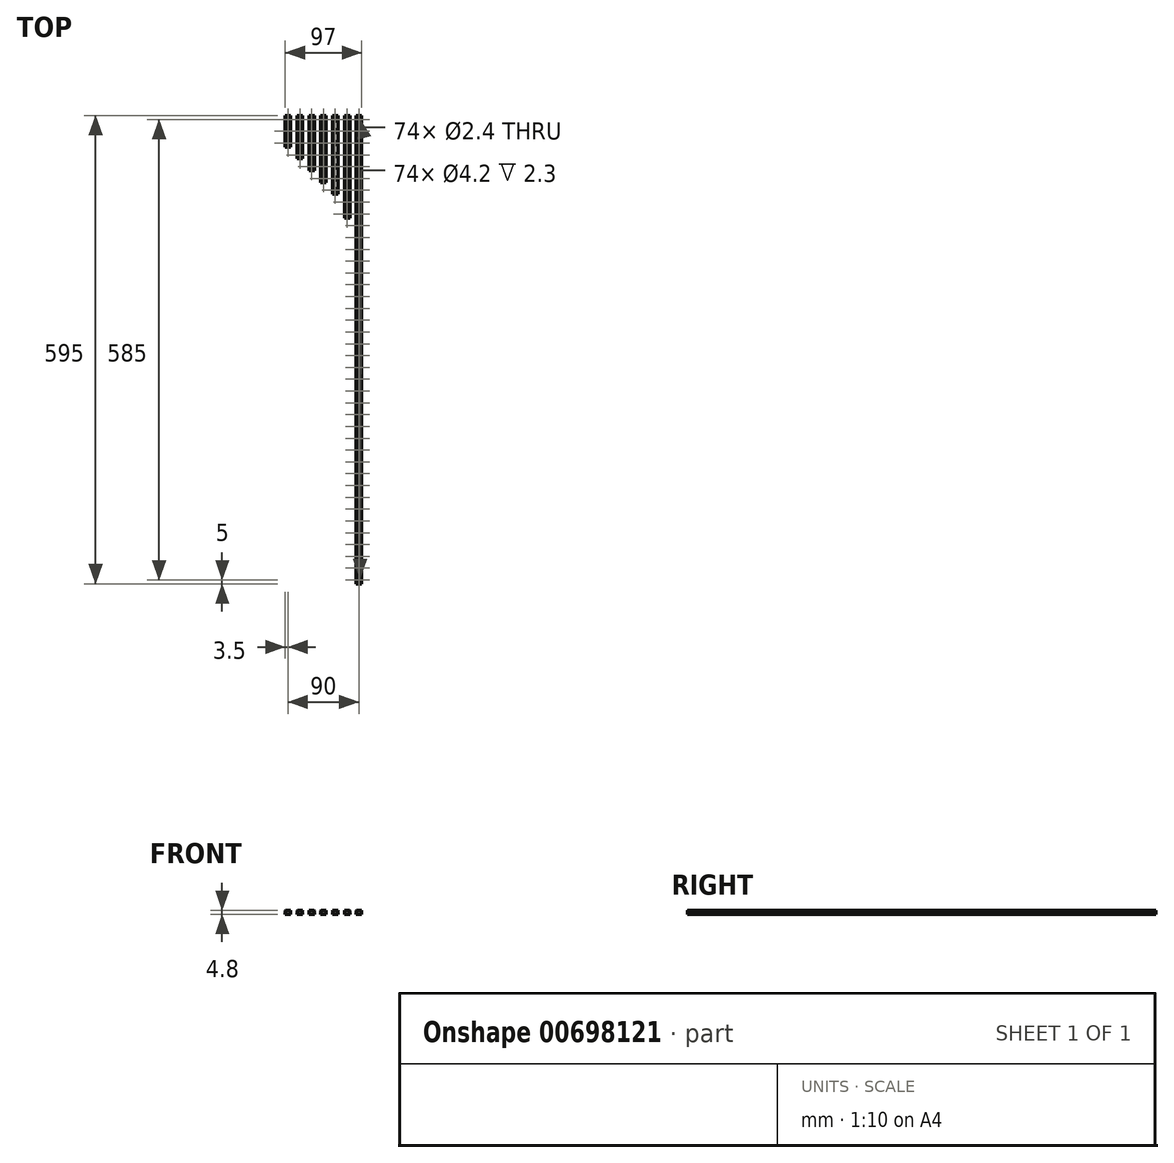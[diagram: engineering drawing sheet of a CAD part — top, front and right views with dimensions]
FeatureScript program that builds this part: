
annotation { "Feature Type Name" : "Feature", "Feature Type Description" : "" }
export const myFeature = defineFeature(function(context is Context, id is Id, definition is map)
    precondition{}
    {
        {
            var Q0;
            Q0=qCreatedBy(makeId("Front.planeOp"),FACE);
            var sketch = newSketch(context, id + "F0", { "sketchPlane" : qUnion([Q0])});
            skPoint(sketch, "E0.middle", {"position": v(0, 0) * mm});
            skLineSegment(sketch, "E1.bottom", {"start": v(3.22, -2.4) * mm, "end": v(-3.22, -2.4) * mm});
            skLineSegment(sketch, "E1.top", {"start": v(3.22, 2.4) * mm, "end": v(-3.22, 2.4) * mm});
            skLineSegment(sketch, "E1.left", {"start": v(3.5, -2.12) * mm, "end": v(3.5, 0.1) * mm});
            skLineSegment(sketch, "E1.right", {"start": v(-3.5, -2.12) * mm, "end": v(-3.5, 0.1) * mm});
            skArc(sketch, "E2", {"start": v(-3.5, 0.1) * mm, "mid": v(-3.23, 0.26) * mm, "end": v(-3.04, 0.51) * mm});
            skArc(sketch, "E3", {"start": v(3.5, 1.58) * mm, "mid": v(3.23, 1.42) * mm, "end": v(3.04, 1.17) * mm});
            skLineSegment(sketch, "E4", {"start": v(2.6, 1.16) * mm, "end": v(3.04, 1.16) * mm});
            skLineSegment(sketch, "E5", {"start": v(2.6, 0.51) * mm, "end": v(3.04, 0.51) * mm});
            skLineSegment(sketch, "E6", {"start": v(-2.6, 0.51) * mm, "end": v(-3.04, 0.51) * mm});
            skLineSegment(sketch, "E7", {"start": v(-2.6, 1.16) * mm, "end": v(-3.04, 1.16) * mm});
            skLineSegment(sketch, "E8", {"start": v(-3.5, 2.12) * mm, "end": v(-3.22, 2.4) * mm});
            skLineSegment(sketch, "E9.MirrorCS", {"start": v(3.5, 2.12) * mm, "end": v(3.22, 2.4) * mm});
            skLineSegment(sketch, "E10.MirrorCS", {"start": v(3.5, -2.12) * mm, "end": v(3.22, -2.4) * mm});
            skLineSegment(sketch, "E11.MirrorCS", {"start": v(-3.5, -2.12) * mm, "end": v(-3.22, -2.4) * mm});
            skPoint(sketch, "E12.orphan", {"position": v(-3.5, 2.4) * mm});
            skLineSegment(sketch, "E13.trimOffspring", {"start": v(-3.5, 1.58) * mm, "end": v(-3.5, 2.12) * mm});
            skArc(sketch, "E14.trimOffspring", {"start": v(-3.04, 1.17) * mm, "mid": v(-3.23, 1.42) * mm, "end": v(-3.5, 1.58) * mm});
            skPoint(sketch, "E15.orphan", {"position": v(3.5, 2.4) * mm});
            skLineSegment(sketch, "E16.trimOffspring", {"start": v(3.5, 1.58) * mm, "end": v(3.5, 2.12) * mm});
            skArc(sketch, "E17.trimOffspring", {"start": v(3.04, 0.51) * mm, "mid": v(3.23, 0.26) * mm, "end": v(3.5, 0.1) * mm});
            skPoint(sketch, "E18.orphan", {"position": v(3.5, -2.4) * mm});
            skPoint(sketch, "E19.orphan", {"position": v(-3.5, -2.4) * mm});
            skLineSegment(sketch, "E20", {"start": v(-2.6, 1.16) * mm, "end": v(-2.6, 0.51) * mm});
            skLineSegment(sketch, "E21", {"start": v(2.6, 1.16) * mm, "end": v(2.6, 0.51) * mm});
            skLineSegment(sketch, "E22", {"start": v(-3.74, 0.84) * mm, "end": v(3.74, 0.84) * mm, "construction": true});
            skLineSegment(sketch, "E23.1.0.0", {"start": v(11.26, 0.84) * mm, "end": v(18.74, 0.84) * mm, "construction": true});
            skLineSegment(sketch, "E23.1.0.1", {"start": v(11.5, -2.12) * mm, "end": v(11.5, 0.1) * mm});
            skLineSegment(sketch, "E23.1.0.2", {"start": v(18.5, -2.12) * mm, "end": v(18.5, 0.1) * mm});
            skLineSegment(sketch, "E23.1.0.3", {"start": v(18.22, -2.4) * mm, "end": v(11.78, -2.4) * mm});
            skLineSegment(sketch, "E23.1.0.4", {"start": v(18.22, 2.4) * mm, "end": v(11.78, 2.4) * mm});
            skPoint(sketch, "E23.1.0.5", {"position": v(15, 0) * mm});
            skPoint(sketch, "E23.1.0.6", {"position": v(11.5, -2.4) * mm});
            skPoint(sketch, "E23.1.0.7", {"position": v(11.5, 2.4) * mm});
            skPoint(sketch, "E23.1.0.8", {"position": v(18.5, 2.4) * mm});
            skPoint(sketch, "E23.1.0.9", {"position": v(18.5, -2.4) * mm});
            skPoint(sketch, "E23.1.0.10", {"position": v(15, 0) * mm});
            skLineSegment(sketch, "E23.1.0.11", {"start": v(18.5, -2.12) * mm, "end": v(18.22, -2.4) * mm});
            skLineSegment(sketch, "E23.1.0.12", {"start": v(18.5, 2.12) * mm, "end": v(18.22, 2.4) * mm});
            skLineSegment(sketch, "E23.1.0.13", {"start": v(11.5, -2.12) * mm, "end": v(11.78, -2.4) * mm});
            skLineSegment(sketch, "E23.1.0.14", {"start": v(12.4, 1.16) * mm, "end": v(11.96, 1.16) * mm});
            skLineSegment(sketch, "E23.1.0.15", {"start": v(11.5, 1.58) * mm, "end": v(11.5, 2.12) * mm});
            skLineSegment(sketch, "E23.1.0.16", {"start": v(18.5, 1.58) * mm, "end": v(18.5, 2.12) * mm});
            skArc(sketch, "E23.1.0.17", {"start": v(18.04, 0.51) * mm, "mid": v(18.23, 0.26) * mm, "end": v(18.5, 0.1) * mm});
            skLineSegment(sketch, "E23.1.0.18", {"start": v(12.4, 1.16) * mm, "end": v(12.4, 0.51) * mm});
            skLineSegment(sketch, "E23.1.0.19", {"start": v(17.6, 0.51) * mm, "end": v(18.04, 0.51) * mm});
            skLineSegment(sketch, "E23.1.0.20", {"start": v(12.4, 0.51) * mm, "end": v(11.96, 0.51) * mm});
            skArc(sketch, "E23.1.0.21", {"start": v(11.5, 0.1) * mm, "mid": v(11.77, 0.26) * mm, "end": v(11.96, 0.51) * mm});
            skLineSegment(sketch, "E23.1.0.22", {"start": v(11.5, 2.12) * mm, "end": v(11.78, 2.4) * mm});
            skArc(sketch, "E23.1.0.23", {"start": v(11.96, 1.17) * mm, "mid": v(11.77, 1.42) * mm, "end": v(11.5, 1.58) * mm});
            skLineSegment(sketch, "E23.1.0.24", {"start": v(17.6, 1.16) * mm, "end": v(18.04, 1.16) * mm});
            skArc(sketch, "E23.1.0.25", {"start": v(18.5, 1.58) * mm, "mid": v(18.23, 1.42) * mm, "end": v(18.04, 1.17) * mm});
            skArc(sketch, "E23.1.0.26", {"start": v(18.04, 0.51) * mm, "mid": v(18.23, 0.26) * mm, "end": v(18.5, 0.1) * mm});
            skLineSegment(sketch, "E23.1.0.27", {"start": v(17.6, 1.16) * mm, "end": v(17.6, 0.51) * mm});
            skLineSegment(sketch, "E23.2.0.0", {"start": v(26.26, 0.84) * mm, "end": v(33.74, 0.84) * mm, "construction": true});
            skLineSegment(sketch, "E23.2.0.1", {"start": v(26.5, -2.12) * mm, "end": v(26.5, 0.1) * mm});
            skLineSegment(sketch, "E23.2.0.2", {"start": v(33.5, -2.12) * mm, "end": v(33.5, 0.1) * mm});
            skLineSegment(sketch, "E23.2.0.3", {"start": v(33.22, -2.4) * mm, "end": v(26.78, -2.4) * mm});
            skLineSegment(sketch, "E23.2.0.4", {"start": v(33.22, 2.4) * mm, "end": v(26.78, 2.4) * mm});
            skPoint(sketch, "E23.2.0.5", {"position": v(30, 0) * mm});
            skPoint(sketch, "E23.2.0.6", {"position": v(26.5, -2.4) * mm});
            skPoint(sketch, "E23.2.0.7", {"position": v(26.5, 2.4) * mm});
            skPoint(sketch, "E23.2.0.8", {"position": v(33.5, 2.4) * mm});
            skPoint(sketch, "E23.2.0.9", {"position": v(33.5, -2.4) * mm});
            skPoint(sketch, "E23.2.0.10", {"position": v(30, 0) * mm});
            skLineSegment(sketch, "E23.2.0.11", {"start": v(33.5, -2.12) * mm, "end": v(33.22, -2.4) * mm});
            skLineSegment(sketch, "E23.2.0.12", {"start": v(33.5, 2.12) * mm, "end": v(33.22, 2.4) * mm});
            skLineSegment(sketch, "E23.2.0.13", {"start": v(26.5, -2.12) * mm, "end": v(26.78, -2.4) * mm});
            skLineSegment(sketch, "E23.2.0.14", {"start": v(27.4, 1.16) * mm, "end": v(26.96, 1.16) * mm});
            skLineSegment(sketch, "E23.2.0.15", {"start": v(26.5, 1.58) * mm, "end": v(26.5, 2.12) * mm});
            skLineSegment(sketch, "E23.2.0.16", {"start": v(33.5, 1.58) * mm, "end": v(33.5, 2.12) * mm});
            skArc(sketch, "E23.2.0.17", {"start": v(33.04, 0.51) * mm, "mid": v(33.23, 0.26) * mm, "end": v(33.5, 0.1) * mm});
            skLineSegment(sketch, "E23.2.0.18", {"start": v(27.4, 1.16) * mm, "end": v(27.4, 0.51) * mm});
            skLineSegment(sketch, "E23.2.0.19", {"start": v(32.6, 0.51) * mm, "end": v(33.04, 0.51) * mm});
            skLineSegment(sketch, "E23.2.0.20", {"start": v(27.4, 0.51) * mm, "end": v(26.96, 0.51) * mm});
            skArc(sketch, "E23.2.0.21", {"start": v(26.5, 0.1) * mm, "mid": v(26.77, 0.26) * mm, "end": v(26.96, 0.51) * mm});
            skLineSegment(sketch, "E23.2.0.22", {"start": v(26.5, 2.12) * mm, "end": v(26.78, 2.4) * mm});
            skArc(sketch, "E23.2.0.23", {"start": v(26.96, 1.17) * mm, "mid": v(26.77, 1.42) * mm, "end": v(26.5, 1.58) * mm});
            skLineSegment(sketch, "E23.2.0.24", {"start": v(32.6, 1.16) * mm, "end": v(33.04, 1.16) * mm});
            skArc(sketch, "E23.2.0.25", {"start": v(33.5, 1.58) * mm, "mid": v(33.23, 1.42) * mm, "end": v(33.04, 1.17) * mm});
            skArc(sketch, "E23.2.0.26", {"start": v(33.04, 0.51) * mm, "mid": v(33.23, 0.26) * mm, "end": v(33.5, 0.1) * mm});
            skLineSegment(sketch, "E23.2.0.27", {"start": v(32.6, 1.16) * mm, "end": v(32.6, 0.51) * mm});
            skLineSegment(sketch, "E23.3.0.0", {"start": v(41.26, 0.84) * mm, "end": v(48.74, 0.84) * mm, "construction": true});
            skLineSegment(sketch, "E23.3.0.1", {"start": v(41.5, -2.12) * mm, "end": v(41.5, 0.1) * mm});
            skLineSegment(sketch, "E23.3.0.2", {"start": v(48.5, -2.12) * mm, "end": v(48.5, 0.1) * mm});
            skLineSegment(sketch, "E23.3.0.3", {"start": v(48.22, -2.4) * mm, "end": v(41.78, -2.4) * mm});
            skLineSegment(sketch, "E23.3.0.4", {"start": v(48.22, 2.4) * mm, "end": v(41.78, 2.4) * mm});
            skPoint(sketch, "E23.3.0.5", {"position": v(45, 0) * mm});
            skPoint(sketch, "E23.3.0.6", {"position": v(41.5, -2.4) * mm});
            skPoint(sketch, "E23.3.0.7", {"position": v(41.5, 2.4) * mm});
            skPoint(sketch, "E23.3.0.8", {"position": v(48.5, 2.4) * mm});
            skPoint(sketch, "E23.3.0.9", {"position": v(48.5, -2.4) * mm});
            skPoint(sketch, "E23.3.0.10", {"position": v(45, 0) * mm});
            skLineSegment(sketch, "E23.3.0.11", {"start": v(48.5, -2.12) * mm, "end": v(48.22, -2.4) * mm});
            skLineSegment(sketch, "E23.3.0.12", {"start": v(48.5, 2.12) * mm, "end": v(48.22, 2.4) * mm});
            skLineSegment(sketch, "E23.3.0.13", {"start": v(41.5, -2.12) * mm, "end": v(41.78, -2.4) * mm});
            skLineSegment(sketch, "E23.3.0.14", {"start": v(42.4, 1.16) * mm, "end": v(41.96, 1.16) * mm});
            skLineSegment(sketch, "E23.3.0.15", {"start": v(41.5, 1.58) * mm, "end": v(41.5, 2.12) * mm});
            skLineSegment(sketch, "E23.3.0.16", {"start": v(48.5, 1.58) * mm, "end": v(48.5, 2.12) * mm});
            skArc(sketch, "E23.3.0.17", {"start": v(48.04, 0.51) * mm, "mid": v(48.23, 0.26) * mm, "end": v(48.5, 0.1) * mm});
            skLineSegment(sketch, "E23.3.0.18", {"start": v(42.4, 1.16) * mm, "end": v(42.4, 0.51) * mm});
            skLineSegment(sketch, "E23.3.0.19", {"start": v(47.6, 0.51) * mm, "end": v(48.04, 0.51) * mm});
            skLineSegment(sketch, "E23.3.0.20", {"start": v(42.4, 0.51) * mm, "end": v(41.96, 0.51) * mm});
            skArc(sketch, "E23.3.0.21", {"start": v(41.5, 0.1) * mm, "mid": v(41.77, 0.26) * mm, "end": v(41.96, 0.51) * mm});
            skLineSegment(sketch, "E23.3.0.22", {"start": v(41.5, 2.12) * mm, "end": v(41.78, 2.4) * mm});
            skArc(sketch, "E23.3.0.23", {"start": v(41.96, 1.17) * mm, "mid": v(41.77, 1.42) * mm, "end": v(41.5, 1.58) * mm});
            skLineSegment(sketch, "E23.3.0.24", {"start": v(47.6, 1.16) * mm, "end": v(48.04, 1.16) * mm});
            skArc(sketch, "E23.3.0.25", {"start": v(48.5, 1.58) * mm, "mid": v(48.23, 1.42) * mm, "end": v(48.04, 1.17) * mm});
            skArc(sketch, "E23.3.0.26", {"start": v(48.04, 0.51) * mm, "mid": v(48.23, 0.26) * mm, "end": v(48.5, 0.1) * mm});
            skLineSegment(sketch, "E23.3.0.27", {"start": v(47.6, 1.16) * mm, "end": v(47.6, 0.51) * mm});
            skLineSegment(sketch, "E23.4.0.0", {"start": v(56.26, 0.84) * mm, "end": v(63.74, 0.84) * mm, "construction": true});
            skLineSegment(sketch, "E23.4.0.1", {"start": v(56.5, -2.12) * mm, "end": v(56.5, 0.1) * mm});
            skLineSegment(sketch, "E23.4.0.2", {"start": v(63.5, -2.12) * mm, "end": v(63.5, 0.1) * mm});
            skLineSegment(sketch, "E23.4.0.3", {"start": v(63.22, -2.4) * mm, "end": v(56.78, -2.4) * mm});
            skLineSegment(sketch, "E23.4.0.4", {"start": v(63.22, 2.4) * mm, "end": v(56.78, 2.4) * mm});
            skPoint(sketch, "E23.4.0.5", {"position": v(60, 0) * mm});
            skPoint(sketch, "E23.4.0.6", {"position": v(56.5, -2.4) * mm});
            skPoint(sketch, "E23.4.0.7", {"position": v(56.5, 2.4) * mm});
            skPoint(sketch, "E23.4.0.8", {"position": v(63.5, 2.4) * mm});
            skPoint(sketch, "E23.4.0.9", {"position": v(63.5, -2.4) * mm});
            skPoint(sketch, "E23.4.0.10", {"position": v(60, 0) * mm});
            skLineSegment(sketch, "E23.4.0.11", {"start": v(63.5, -2.12) * mm, "end": v(63.22, -2.4) * mm});
            skLineSegment(sketch, "E23.4.0.12", {"start": v(63.5, 2.12) * mm, "end": v(63.22, 2.4) * mm});
            skLineSegment(sketch, "E23.4.0.13", {"start": v(56.5, -2.12) * mm, "end": v(56.78, -2.4) * mm});
            skLineSegment(sketch, "E23.4.0.14", {"start": v(57.4, 1.16) * mm, "end": v(56.96, 1.16) * mm});
            skLineSegment(sketch, "E23.4.0.15", {"start": v(56.5, 1.58) * mm, "end": v(56.5, 2.12) * mm});
            skLineSegment(sketch, "E23.4.0.16", {"start": v(63.5, 1.58) * mm, "end": v(63.5, 2.12) * mm});
            skArc(sketch, "E23.4.0.17", {"start": v(63.04, 0.51) * mm, "mid": v(63.23, 0.26) * mm, "end": v(63.5, 0.1) * mm});
            skLineSegment(sketch, "E23.4.0.18", {"start": v(57.4, 1.16) * mm, "end": v(57.4, 0.51) * mm});
            skLineSegment(sketch, "E23.4.0.19", {"start": v(62.6, 0.51) * mm, "end": v(63.04, 0.51) * mm});
            skLineSegment(sketch, "E23.4.0.20", {"start": v(57.4, 0.51) * mm, "end": v(56.96, 0.51) * mm});
            skArc(sketch, "E23.4.0.21", {"start": v(56.5, 0.1) * mm, "mid": v(56.77, 0.26) * mm, "end": v(56.96, 0.51) * mm});
            skLineSegment(sketch, "E23.4.0.22", {"start": v(56.5, 2.12) * mm, "end": v(56.78, 2.4) * mm});
            skArc(sketch, "E23.4.0.23", {"start": v(56.96, 1.17) * mm, "mid": v(56.77, 1.42) * mm, "end": v(56.5, 1.58) * mm});
            skLineSegment(sketch, "E23.4.0.24", {"start": v(62.6, 1.16) * mm, "end": v(63.04, 1.16) * mm});
            skArc(sketch, "E23.4.0.25", {"start": v(63.5, 1.58) * mm, "mid": v(63.23, 1.42) * mm, "end": v(63.04, 1.17) * mm});
            skArc(sketch, "E23.4.0.26", {"start": v(63.04, 0.51) * mm, "mid": v(63.23, 0.26) * mm, "end": v(63.5, 0.1) * mm});
            skLineSegment(sketch, "E23.4.0.27", {"start": v(62.6, 1.16) * mm, "end": v(62.6, 0.51) * mm});
            skLineSegment(sketch, "E23.5.0.0", {"start": v(71.26, 0.84) * mm, "end": v(78.74, 0.84) * mm, "construction": true});
            skLineSegment(sketch, "E23.5.0.1", {"start": v(71.5, -2.12) * mm, "end": v(71.5, 0.1) * mm});
            skLineSegment(sketch, "E23.5.0.2", {"start": v(78.5, -2.12) * mm, "end": v(78.5, 0.1) * mm});
            skLineSegment(sketch, "E23.5.0.3", {"start": v(78.22, -2.4) * mm, "end": v(71.78, -2.4) * mm});
            skLineSegment(sketch, "E23.5.0.4", {"start": v(78.22, 2.4) * mm, "end": v(71.78, 2.4) * mm});
            skPoint(sketch, "E23.5.0.5", {"position": v(75, 0) * mm});
            skPoint(sketch, "E23.5.0.6", {"position": v(71.5, -2.4) * mm});
            skPoint(sketch, "E23.5.0.7", {"position": v(71.5, 2.4) * mm});
            skPoint(sketch, "E23.5.0.8", {"position": v(78.5, 2.4) * mm});
            skPoint(sketch, "E23.5.0.9", {"position": v(78.5, -2.4) * mm});
            skPoint(sketch, "E23.5.0.10", {"position": v(75, 0) * mm});
            skLineSegment(sketch, "E23.5.0.11", {"start": v(78.5, -2.12) * mm, "end": v(78.22, -2.4) * mm});
            skLineSegment(sketch, "E23.5.0.12", {"start": v(78.5, 2.12) * mm, "end": v(78.22, 2.4) * mm});
            skLineSegment(sketch, "E23.5.0.13", {"start": v(71.5, -2.12) * mm, "end": v(71.78, -2.4) * mm});
            skLineSegment(sketch, "E23.5.0.14", {"start": v(72.4, 1.16) * mm, "end": v(71.96, 1.16) * mm});
            skLineSegment(sketch, "E23.5.0.15", {"start": v(71.5, 1.58) * mm, "end": v(71.5, 2.12) * mm});
            skLineSegment(sketch, "E23.5.0.16", {"start": v(78.5, 1.58) * mm, "end": v(78.5, 2.12) * mm});
            skArc(sketch, "E23.5.0.17", {"start": v(78.04, 0.51) * mm, "mid": v(78.23, 0.26) * mm, "end": v(78.5, 0.1) * mm});
            skLineSegment(sketch, "E23.5.0.18", {"start": v(72.4, 1.16) * mm, "end": v(72.4, 0.51) * mm});
            skLineSegment(sketch, "E23.5.0.19", {"start": v(77.6, 0.51) * mm, "end": v(78.04, 0.51) * mm});
            skLineSegment(sketch, "E23.5.0.20", {"start": v(72.4, 0.51) * mm, "end": v(71.96, 0.51) * mm});
            skArc(sketch, "E23.5.0.21", {"start": v(71.5, 0.1) * mm, "mid": v(71.77, 0.26) * mm, "end": v(71.96, 0.51) * mm});
            skLineSegment(sketch, "E23.5.0.22", {"start": v(71.5, 2.12) * mm, "end": v(71.78, 2.4) * mm});
            skArc(sketch, "E23.5.0.23", {"start": v(71.96, 1.17) * mm, "mid": v(71.77, 1.42) * mm, "end": v(71.5, 1.58) * mm});
            skLineSegment(sketch, "E23.5.0.24", {"start": v(77.6, 1.16) * mm, "end": v(78.04, 1.16) * mm});
            skArc(sketch, "E23.5.0.25", {"start": v(78.5, 1.58) * mm, "mid": v(78.23, 1.42) * mm, "end": v(78.04, 1.17) * mm});
            skArc(sketch, "E23.5.0.26", {"start": v(78.04, 0.51) * mm, "mid": v(78.23, 0.26) * mm, "end": v(78.5, 0.1) * mm});
            skLineSegment(sketch, "E23.5.0.27", {"start": v(77.6, 1.16) * mm, "end": v(77.6, 0.51) * mm});
            skLineSegment(sketch, "E23.6.0.0", {"start": v(86.26, 0.84) * mm, "end": v(93.74, 0.84) * mm, "construction": true});
            skLineSegment(sketch, "E23.6.0.1", {"start": v(86.5, -2.12) * mm, "end": v(86.5, 0.1) * mm});
            skLineSegment(sketch, "E23.6.0.2", {"start": v(93.5, -2.12) * mm, "end": v(93.5, 0.1) * mm});
            skLineSegment(sketch, "E23.6.0.3", {"start": v(93.22, -2.4) * mm, "end": v(86.78, -2.4) * mm});
            skLineSegment(sketch, "E23.6.0.4", {"start": v(93.22, 2.4) * mm, "end": v(86.78, 2.4) * mm});
            skPoint(sketch, "E23.6.0.5", {"position": v(90, 0) * mm});
            skPoint(sketch, "E23.6.0.6", {"position": v(86.5, -2.4) * mm});
            skPoint(sketch, "E23.6.0.7", {"position": v(86.5, 2.4) * mm});
            skPoint(sketch, "E23.6.0.8", {"position": v(93.5, 2.4) * mm});
            skPoint(sketch, "E23.6.0.9", {"position": v(93.5, -2.4) * mm});
            skPoint(sketch, "E23.6.0.10", {"position": v(90, 0) * mm});
            skLineSegment(sketch, "E23.6.0.11", {"start": v(93.5, -2.12) * mm, "end": v(93.22, -2.4) * mm});
            skLineSegment(sketch, "E23.6.0.12", {"start": v(93.5, 2.12) * mm, "end": v(93.22, 2.4) * mm});
            skLineSegment(sketch, "E23.6.0.13", {"start": v(86.5, -2.12) * mm, "end": v(86.78, -2.4) * mm});
            skLineSegment(sketch, "E23.6.0.14", {"start": v(87.4, 1.16) * mm, "end": v(86.96, 1.16) * mm});
            skLineSegment(sketch, "E23.6.0.15", {"start": v(86.5, 1.58) * mm, "end": v(86.5, 2.12) * mm});
            skLineSegment(sketch, "E23.6.0.16", {"start": v(93.5, 1.58) * mm, "end": v(93.5, 2.12) * mm});
            skArc(sketch, "E23.6.0.17", {"start": v(93.04, 0.51) * mm, "mid": v(93.23, 0.26) * mm, "end": v(93.5, 0.1) * mm});
            skLineSegment(sketch, "E23.6.0.18", {"start": v(87.4, 1.16) * mm, "end": v(87.4, 0.51) * mm});
            skLineSegment(sketch, "E23.6.0.19", {"start": v(92.6, 0.51) * mm, "end": v(93.04, 0.51) * mm});
            skLineSegment(sketch, "E23.6.0.20", {"start": v(87.4, 0.51) * mm, "end": v(86.96, 0.51) * mm});
            skArc(sketch, "E23.6.0.21", {"start": v(86.5, 0.1) * mm, "mid": v(86.77, 0.26) * mm, "end": v(86.96, 0.51) * mm});
            skLineSegment(sketch, "E23.6.0.22", {"start": v(86.5, 2.12) * mm, "end": v(86.78, 2.4) * mm});
            skArc(sketch, "E23.6.0.23", {"start": v(86.96, 1.17) * mm, "mid": v(86.77, 1.42) * mm, "end": v(86.5, 1.58) * mm});
            skLineSegment(sketch, "E23.6.0.24", {"start": v(92.6, 1.16) * mm, "end": v(93.04, 1.16) * mm});
            skArc(sketch, "E23.6.0.25", {"start": v(93.5, 1.58) * mm, "mid": v(93.23, 1.42) * mm, "end": v(93.04, 1.17) * mm});
            skArc(sketch, "E23.6.0.26", {"start": v(93.04, 0.51) * mm, "mid": v(93.23, 0.26) * mm, "end": v(93.5, 0.1) * mm});
            skLineSegment(sketch, "E23.6.0.27", {"start": v(92.6, 1.16) * mm, "end": v(92.6, 0.51) * mm});
            skLineSegment(sketch, "E23.direction1", {"start": v(-3.5, -2.4) * mm, "end": v(11.5, -2.4) * mm, "construction": true});
            skSolve(sketch);
        }
        {
            var Q0;
            Q0=makeQuery(id+"F0.imprint","IMPRINT",FACE,{"disambiguationData":[TD([[makeQuery(id+"F0.imprint","IMPRINT",EDGE,{"derivedFrom":sQuery(id+"F0.wireOp",EDGE,"E1.bottom")}),-1.0]])]});
            extrude(context, id + "F1", {"entities" : qUnion([Q0]), "depth" : 40 * mm, "offsetDistance" : 25 * mm});
        }
        {
            var Q0;
            Q0=makeQuery(id+"F0.imprint","IMPRINT",FACE,{"disambiguationData":[TD([[makeQuery(id+"F0.imprint","IMPRINT",EDGE,{"derivedFrom":sQuery(id+"F0.wireOp",EDGE,"E23.1.0.1")}),-1.0]])]});
            extrude(context, id + "F2", {"entities" : qUnion([Q0]), "depth" : 55 * mm, "offsetDistance" : 25 * mm});
        }
        {
            var Q0;
            Q0=makeQuery(id+"F0.imprint","IMPRINT",FACE,{"disambiguationData":[TD([[makeQuery(id+"F0.imprint","IMPRINT",EDGE,{"derivedFrom":sQuery(id+"F0.wireOp",EDGE,"E23.2.0.1")}),-1.0]])]});
            extrude(context, id + "F3", {"entities" : qUnion([Q0]), "depth" : 70 * mm, "offsetDistance" : 25 * mm});
        }
        {
            var Q0;
            Q0=makeQuery(id+"F0.imprint","IMPRINT",FACE,{"disambiguationData":[TD([[makeQuery(id+"F0.imprint","IMPRINT",EDGE,{"derivedFrom":sQuery(id+"F0.wireOp",EDGE,"E23.3.0.1")}),-1.0]])]});
            extrude(context, id + "F4", {"entities" : qUnion([Q0]), "depth" : 85 * mm, "offsetDistance" : 25 * mm});
        }
        {
            var Q0;
            Q0=makeQuery(id+"F0.imprint","IMPRINT",FACE,{"disambiguationData":[TD([[makeQuery(id+"F0.imprint","IMPRINT",EDGE,{"derivedFrom":sQuery(id+"F0.wireOp",EDGE,"E23.4.0.1")}),-1.0]])]});
            extrude(context, id + "F5", {"entities" : qUnion([Q0]), "depth" : 100 * mm, "offsetDistance" : 25 * mm});
        }
        {
            var Q0;
            Q0=makeQuery(id+"F0.imprint","IMPRINT",FACE,{"disambiguationData":[TD([[makeQuery(id+"F0.imprint","IMPRINT",EDGE,{"derivedFrom":sQuery(id+"F0.wireOp",EDGE,"E23.5.0.1")}),-1.0]])]});
            extrude(context, id + "F6", {"entities" : qUnion([Q0]), "depth" : 130 * mm, "offsetDistance" : 25 * mm});
        }
        {
            var Q0;
            Q0=makeQuery(id+"F0.imprint","IMPRINT",FACE,{"disambiguationData":[TD([[makeQuery(id+"F0.imprint","IMPRINT",EDGE,{"derivedFrom":sQuery(id+"F0.wireOp",EDGE,"E23.6.0.1")}),-1.0]])]});
            extrude(context, id + "F7", {"entities" : qUnion([Q0]), "depth" : 595 * mm, "offsetDistance" : 25 * mm});
        }
        {
            var Q0;
            Q0=makeQuery(id+"F1.opExtrude","SWEPT_FACE",FACE,{"disambiguationData":[OSD([sQuery(id+"F0.wireOp",EDGE,"E1.top")])]});
            var sketch = newSketch(context, id + "F8", { "sketchPlane" : qUnion([Q0])});
            skPoint(sketch, "E24", {"position": v(0, -5) * mm});
            skPoint(sketch, "E25.1.0.0", {"position": v(15, -5) * mm});
            skPoint(sketch, "E25.2.0.0", {"position": v(30, -5) * mm});
            skPoint(sketch, "E25.3.0.0", {"position": v(45, -5) * mm});
            skPoint(sketch, "E25.4.0.0", {"position": v(60, -5) * mm});
            skPoint(sketch, "E25.5.0.0", {"position": v(75, -5) * mm});
            skPoint(sketch, "E25.6.0.0", {"position": v(90, -5) * mm});
            skLineSegment(sketch, "E25.direction1", {"start": v(0, -5) * mm, "end": v(15, -5) * mm, "construction": true});
            skPoint(sketch, "E26.1.0.0", {"position": v(0, -20) * mm});
            skPoint(sketch, "E26.1.0.1", {"position": v(15, -20) * mm});
            skPoint(sketch, "E26.1.0.2", {"position": v(30, -20) * mm});
            skPoint(sketch, "E26.1.0.3", {"position": v(45, -20) * mm});
            skPoint(sketch, "E26.1.0.4", {"position": v(60, -20) * mm});
            skPoint(sketch, "E26.1.0.5", {"position": v(75, -20) * mm});
            skPoint(sketch, "E26.1.0.6", {"position": v(90, -20) * mm});
            skPoint(sketch, "E26.2.0.0", {"position": v(0, -35) * mm});
            skPoint(sketch, "E26.2.0.1", {"position": v(15, -35) * mm});
            skPoint(sketch, "E26.2.0.2", {"position": v(30, -35) * mm});
            skPoint(sketch, "E26.2.0.3", {"position": v(45, -35) * mm});
            skPoint(sketch, "E26.2.0.4", {"position": v(60, -35) * mm});
            skPoint(sketch, "E26.2.0.5", {"position": v(75, -35) * mm});
            skPoint(sketch, "E26.2.0.6", {"position": v(90, -35) * mm});
            skPoint(sketch, "E26.3.0.0", {"position": v(0, -50) * mm});
            skPoint(sketch, "E26.3.0.1", {"position": v(15, -50) * mm});
            skPoint(sketch, "E26.3.0.2", {"position": v(30, -50) * mm});
            skPoint(sketch, "E26.3.0.3", {"position": v(45, -50) * mm});
            skPoint(sketch, "E26.3.0.4", {"position": v(60, -50) * mm});
            skPoint(sketch, "E26.3.0.5", {"position": v(75, -50) * mm});
            skPoint(sketch, "E26.3.0.6", {"position": v(90, -50) * mm});
            skPoint(sketch, "E26.4.0.0", {"position": v(0, -65) * mm});
            skPoint(sketch, "E26.4.0.1", {"position": v(15, -65) * mm});
            skPoint(sketch, "E26.4.0.2", {"position": v(30, -65) * mm});
            skPoint(sketch, "E26.4.0.3", {"position": v(45, -65) * mm});
            skPoint(sketch, "E26.4.0.4", {"position": v(60, -65) * mm});
            skPoint(sketch, "E26.4.0.5", {"position": v(75, -65) * mm});
            skPoint(sketch, "E26.4.0.6", {"position": v(90, -65) * mm});
            skPoint(sketch, "E26.5.0.0", {"position": v(0, -80) * mm});
            skPoint(sketch, "E26.5.0.1", {"position": v(15, -80) * mm});
            skPoint(sketch, "E26.5.0.2", {"position": v(30, -80) * mm});
            skPoint(sketch, "E26.5.0.3", {"position": v(45, -80) * mm});
            skPoint(sketch, "E26.5.0.4", {"position": v(60, -80) * mm});
            skPoint(sketch, "E26.5.0.5", {"position": v(75, -80) * mm});
            skPoint(sketch, "E26.5.0.6", {"position": v(90, -80) * mm});
            skPoint(sketch, "E26.6.0.0", {"position": v(0, -95) * mm});
            skPoint(sketch, "E26.6.0.1", {"position": v(15, -95) * mm});
            skPoint(sketch, "E26.6.0.2", {"position": v(30, -95) * mm});
            skPoint(sketch, "E26.6.0.3", {"position": v(45, -95) * mm});
            skPoint(sketch, "E26.6.0.4", {"position": v(60, -95) * mm});
            skPoint(sketch, "E26.6.0.5", {"position": v(75, -95) * mm});
            skPoint(sketch, "E26.6.0.6", {"position": v(90, -95) * mm});
            skPoint(sketch, "E26.7.0.0", {"position": v(0, -110) * mm});
            skPoint(sketch, "E26.7.0.1", {"position": v(15, -110) * mm});
            skPoint(sketch, "E26.7.0.2", {"position": v(30, -110) * mm});
            skPoint(sketch, "E26.7.0.3", {"position": v(45, -110) * mm});
            skPoint(sketch, "E26.7.0.4", {"position": v(60, -110) * mm});
            skPoint(sketch, "E26.7.0.5", {"position": v(75, -110) * mm});
            skPoint(sketch, "E26.7.0.6", {"position": v(90, -110) * mm});
            skPoint(sketch, "E26.8.0.0", {"position": v(0, -125) * mm});
            skPoint(sketch, "E26.8.0.1", {"position": v(15, -125) * mm});
            skPoint(sketch, "E26.8.0.2", {"position": v(30, -125) * mm});
            skPoint(sketch, "E26.8.0.3", {"position": v(45, -125) * mm});
            skPoint(sketch, "E26.8.0.4", {"position": v(60, -125) * mm});
            skPoint(sketch, "E26.8.0.5", {"position": v(75, -125) * mm});
            skPoint(sketch, "E26.8.0.6", {"position": v(90, -125) * mm});
            skPoint(sketch, "E26.9.0.0", {"position": v(0, -140) * mm});
            skPoint(sketch, "E26.9.0.1", {"position": v(15, -140) * mm});
            skPoint(sketch, "E26.9.0.2", {"position": v(30, -140) * mm});
            skPoint(sketch, "E26.9.0.3", {"position": v(45, -140) * mm});
            skPoint(sketch, "E26.9.0.4", {"position": v(60, -140) * mm});
            skPoint(sketch, "E26.9.0.5", {"position": v(75, -140) * mm});
            skPoint(sketch, "E26.9.0.6", {"position": v(90, -140) * mm});
            skPoint(sketch, "E26.10.0.0", {"position": v(0, -155) * mm});
            skPoint(sketch, "E26.10.0.1", {"position": v(15, -155) * mm});
            skPoint(sketch, "E26.10.0.2", {"position": v(30, -155) * mm});
            skPoint(sketch, "E26.10.0.3", {"position": v(45, -155) * mm});
            skPoint(sketch, "E26.10.0.4", {"position": v(60, -155) * mm});
            skPoint(sketch, "E26.10.0.5", {"position": v(75, -155) * mm});
            skPoint(sketch, "E26.10.0.6", {"position": v(90, -155) * mm});
            skPoint(sketch, "E26.11.0.0", {"position": v(0, -170) * mm});
            skPoint(sketch, "E26.11.0.1", {"position": v(15, -170) * mm});
            skPoint(sketch, "E26.11.0.2", {"position": v(30, -170) * mm});
            skPoint(sketch, "E26.11.0.3", {"position": v(45, -170) * mm});
            skPoint(sketch, "E26.11.0.4", {"position": v(60, -170) * mm});
            skPoint(sketch, "E26.11.0.5", {"position": v(75, -170) * mm});
            skPoint(sketch, "E26.11.0.6", {"position": v(90, -170) * mm});
            skPoint(sketch, "E26.12.0.0", {"position": v(0, -185) * mm});
            skPoint(sketch, "E26.12.0.1", {"position": v(15, -185) * mm});
            skPoint(sketch, "E26.12.0.2", {"position": v(30, -185) * mm});
            skPoint(sketch, "E26.12.0.3", {"position": v(45, -185) * mm});
            skPoint(sketch, "E26.12.0.4", {"position": v(60, -185) * mm});
            skPoint(sketch, "E26.12.0.5", {"position": v(75, -185) * mm});
            skPoint(sketch, "E26.12.0.6", {"position": v(90, -185) * mm});
            skPoint(sketch, "E26.13.0.0", {"position": v(0, -200) * mm});
            skPoint(sketch, "E26.13.0.1", {"position": v(15, -200) * mm});
            skPoint(sketch, "E26.13.0.2", {"position": v(30, -200) * mm});
            skPoint(sketch, "E26.13.0.3", {"position": v(45, -200) * mm});
            skPoint(sketch, "E26.13.0.4", {"position": v(60, -200) * mm});
            skPoint(sketch, "E26.13.0.5", {"position": v(75, -200) * mm});
            skPoint(sketch, "E26.13.0.6", {"position": v(90, -200) * mm});
            skPoint(sketch, "E26.14.0.0", {"position": v(0, -215) * mm});
            skPoint(sketch, "E26.14.0.1", {"position": v(15, -215) * mm});
            skPoint(sketch, "E26.14.0.2", {"position": v(30, -215) * mm});
            skPoint(sketch, "E26.14.0.3", {"position": v(45, -215) * mm});
            skPoint(sketch, "E26.14.0.4", {"position": v(60, -215) * mm});
            skPoint(sketch, "E26.14.0.5", {"position": v(75, -215) * mm});
            skPoint(sketch, "E26.14.0.6", {"position": v(90, -215) * mm});
            skPoint(sketch, "E26.15.0.0", {"position": v(0, -230) * mm});
            skPoint(sketch, "E26.15.0.1", {"position": v(15, -230) * mm});
            skPoint(sketch, "E26.15.0.2", {"position": v(30, -230) * mm});
            skPoint(sketch, "E26.15.0.3", {"position": v(45, -230) * mm});
            skPoint(sketch, "E26.15.0.4", {"position": v(60, -230) * mm});
            skPoint(sketch, "E26.15.0.5", {"position": v(75, -230) * mm});
            skPoint(sketch, "E26.15.0.6", {"position": v(90, -230) * mm});
            skPoint(sketch, "E26.16.0.0", {"position": v(0, -245) * mm});
            skPoint(sketch, "E26.16.0.1", {"position": v(15, -245) * mm});
            skPoint(sketch, "E26.16.0.2", {"position": v(30, -245) * mm});
            skPoint(sketch, "E26.16.0.3", {"position": v(45, -245) * mm});
            skPoint(sketch, "E26.16.0.4", {"position": v(60, -245) * mm});
            skPoint(sketch, "E26.16.0.5", {"position": v(75, -245) * mm});
            skPoint(sketch, "E26.16.0.6", {"position": v(90, -245) * mm});
            skPoint(sketch, "E26.17.0.0", {"position": v(0, -260) * mm});
            skPoint(sketch, "E26.17.0.1", {"position": v(15, -260) * mm});
            skPoint(sketch, "E26.17.0.2", {"position": v(30, -260) * mm});
            skPoint(sketch, "E26.17.0.3", {"position": v(45, -260) * mm});
            skPoint(sketch, "E26.17.0.4", {"position": v(60, -260) * mm});
            skPoint(sketch, "E26.17.0.5", {"position": v(75, -260) * mm});
            skPoint(sketch, "E26.17.0.6", {"position": v(90, -260) * mm});
            skPoint(sketch, "E26.18.0.0", {"position": v(0, -275) * mm});
            skPoint(sketch, "E26.18.0.1", {"position": v(15, -275) * mm});
            skPoint(sketch, "E26.18.0.2", {"position": v(30, -275) * mm});
            skPoint(sketch, "E26.18.0.3", {"position": v(45, -275) * mm});
            skPoint(sketch, "E26.18.0.4", {"position": v(60, -275) * mm});
            skPoint(sketch, "E26.18.0.5", {"position": v(75, -275) * mm});
            skPoint(sketch, "E26.18.0.6", {"position": v(90, -275) * mm});
            skPoint(sketch, "E26.19.0.0", {"position": v(0, -290) * mm});
            skPoint(sketch, "E26.19.0.1", {"position": v(15, -290) * mm});
            skPoint(sketch, "E26.19.0.2", {"position": v(30, -290) * mm});
            skPoint(sketch, "E26.19.0.3", {"position": v(45, -290) * mm});
            skPoint(sketch, "E26.19.0.4", {"position": v(60, -290) * mm});
            skPoint(sketch, "E26.19.0.5", {"position": v(75, -290) * mm});
            skPoint(sketch, "E26.19.0.6", {"position": v(90, -290) * mm});
            skPoint(sketch, "E26.20.0.0", {"position": v(0, -305) * mm});
            skPoint(sketch, "E26.20.0.1", {"position": v(15, -305) * mm});
            skPoint(sketch, "E26.20.0.2", {"position": v(30, -305) * mm});
            skPoint(sketch, "E26.20.0.3", {"position": v(45, -305) * mm});
            skPoint(sketch, "E26.20.0.4", {"position": v(60, -305) * mm});
            skPoint(sketch, "E26.20.0.5", {"position": v(75, -305) * mm});
            skPoint(sketch, "E26.20.0.6", {"position": v(90, -305) * mm});
            skPoint(sketch, "E26.21.0.0", {"position": v(0, -320) * mm});
            skPoint(sketch, "E26.21.0.1", {"position": v(15, -320) * mm});
            skPoint(sketch, "E26.21.0.2", {"position": v(30, -320) * mm});
            skPoint(sketch, "E26.21.0.3", {"position": v(45, -320) * mm});
            skPoint(sketch, "E26.21.0.4", {"position": v(60, -320) * mm});
            skPoint(sketch, "E26.21.0.5", {"position": v(75, -320) * mm});
            skPoint(sketch, "E26.21.0.6", {"position": v(90, -320) * mm});
            skPoint(sketch, "E26.22.0.0", {"position": v(0, -335) * mm});
            skPoint(sketch, "E26.22.0.1", {"position": v(15, -335) * mm});
            skPoint(sketch, "E26.22.0.2", {"position": v(30, -335) * mm});
            skPoint(sketch, "E26.22.0.3", {"position": v(45, -335) * mm});
            skPoint(sketch, "E26.22.0.4", {"position": v(60, -335) * mm});
            skPoint(sketch, "E26.22.0.5", {"position": v(75, -335) * mm});
            skPoint(sketch, "E26.22.0.6", {"position": v(90, -335) * mm});
            skPoint(sketch, "E26.23.0.0", {"position": v(0, -350) * mm});
            skPoint(sketch, "E26.23.0.1", {"position": v(15, -350) * mm});
            skPoint(sketch, "E26.23.0.2", {"position": v(30, -350) * mm});
            skPoint(sketch, "E26.23.0.3", {"position": v(45, -350) * mm});
            skPoint(sketch, "E26.23.0.4", {"position": v(60, -350) * mm});
            skPoint(sketch, "E26.23.0.5", {"position": v(75, -350) * mm});
            skPoint(sketch, "E26.23.0.6", {"position": v(90, -350) * mm});
            skPoint(sketch, "E26.24.0.0", {"position": v(0, -365) * mm});
            skPoint(sketch, "E26.24.0.1", {"position": v(15, -365) * mm});
            skPoint(sketch, "E26.24.0.2", {"position": v(30, -365) * mm});
            skPoint(sketch, "E26.24.0.3", {"position": v(45, -365) * mm});
            skPoint(sketch, "E26.24.0.4", {"position": v(60, -365) * mm});
            skPoint(sketch, "E26.24.0.5", {"position": v(75, -365) * mm});
            skPoint(sketch, "E26.24.0.6", {"position": v(90, -365) * mm});
            skPoint(sketch, "E26.25.0.0", {"position": v(0, -380) * mm});
            skPoint(sketch, "E26.25.0.1", {"position": v(15, -380) * mm});
            skPoint(sketch, "E26.25.0.2", {"position": v(30, -380) * mm});
            skPoint(sketch, "E26.25.0.3", {"position": v(45, -380) * mm});
            skPoint(sketch, "E26.25.0.4", {"position": v(60, -380) * mm});
            skPoint(sketch, "E26.25.0.5", {"position": v(75, -380) * mm});
            skPoint(sketch, "E26.25.0.6", {"position": v(90, -380) * mm});
            skPoint(sketch, "E26.26.0.0", {"position": v(0, -395) * mm});
            skPoint(sketch, "E26.26.0.1", {"position": v(15, -395) * mm});
            skPoint(sketch, "E26.26.0.2", {"position": v(30, -395) * mm});
            skPoint(sketch, "E26.26.0.3", {"position": v(45, -395) * mm});
            skPoint(sketch, "E26.26.0.4", {"position": v(60, -395) * mm});
            skPoint(sketch, "E26.26.0.5", {"position": v(75, -395) * mm});
            skPoint(sketch, "E26.26.0.6", {"position": v(90, -395) * mm});
            skPoint(sketch, "E26.27.0.0", {"position": v(0, -410) * mm});
            skPoint(sketch, "E26.27.0.1", {"position": v(15, -410) * mm});
            skPoint(sketch, "E26.27.0.2", {"position": v(30, -410) * mm});
            skPoint(sketch, "E26.27.0.3", {"position": v(45, -410) * mm});
            skPoint(sketch, "E26.27.0.4", {"position": v(60, -410) * mm});
            skPoint(sketch, "E26.27.0.5", {"position": v(75, -410) * mm});
            skPoint(sketch, "E26.27.0.6", {"position": v(90, -410) * mm});
            skPoint(sketch, "E26.28.0.0", {"position": v(0, -425) * mm});
            skPoint(sketch, "E26.28.0.1", {"position": v(15, -425) * mm});
            skPoint(sketch, "E26.28.0.2", {"position": v(30, -425) * mm});
            skPoint(sketch, "E26.28.0.3", {"position": v(45, -425) * mm});
            skPoint(sketch, "E26.28.0.4", {"position": v(60, -425) * mm});
            skPoint(sketch, "E26.28.0.5", {"position": v(75, -425) * mm});
            skPoint(sketch, "E26.28.0.6", {"position": v(90, -425) * mm});
            skPoint(sketch, "E26.29.0.0", {"position": v(0, -440) * mm});
            skPoint(sketch, "E26.29.0.1", {"position": v(15, -440) * mm});
            skPoint(sketch, "E26.29.0.2", {"position": v(30, -440) * mm});
            skPoint(sketch, "E26.29.0.3", {"position": v(45, -440) * mm});
            skPoint(sketch, "E26.29.0.4", {"position": v(60, -440) * mm});
            skPoint(sketch, "E26.29.0.5", {"position": v(75, -440) * mm});
            skPoint(sketch, "E26.29.0.6", {"position": v(90, -440) * mm});
            skPoint(sketch, "E26.30.0.0", {"position": v(0, -455) * mm});
            skPoint(sketch, "E26.30.0.1", {"position": v(15, -455) * mm});
            skPoint(sketch, "E26.30.0.2", {"position": v(30, -455) * mm});
            skPoint(sketch, "E26.30.0.3", {"position": v(45, -455) * mm});
            skPoint(sketch, "E26.30.0.4", {"position": v(60, -455) * mm});
            skPoint(sketch, "E26.30.0.5", {"position": v(75, -455) * mm});
            skPoint(sketch, "E26.30.0.6", {"position": v(90, -455) * mm});
            skPoint(sketch, "E26.31.0.0", {"position": v(0, -470) * mm});
            skPoint(sketch, "E26.31.0.1", {"position": v(15, -470) * mm});
            skPoint(sketch, "E26.31.0.2", {"position": v(30, -470) * mm});
            skPoint(sketch, "E26.31.0.3", {"position": v(45, -470) * mm});
            skPoint(sketch, "E26.31.0.4", {"position": v(60, -470) * mm});
            skPoint(sketch, "E26.31.0.5", {"position": v(75, -470) * mm});
            skPoint(sketch, "E26.31.0.6", {"position": v(90, -470) * mm});
            skPoint(sketch, "E26.32.0.0", {"position": v(0, -485) * mm});
            skPoint(sketch, "E26.32.0.1", {"position": v(15, -485) * mm});
            skPoint(sketch, "E26.32.0.2", {"position": v(30, -485) * mm});
            skPoint(sketch, "E26.32.0.3", {"position": v(45, -485) * mm});
            skPoint(sketch, "E26.32.0.4", {"position": v(60, -485) * mm});
            skPoint(sketch, "E26.32.0.5", {"position": v(75, -485) * mm});
            skPoint(sketch, "E26.32.0.6", {"position": v(90, -485) * mm});
            skPoint(sketch, "E26.33.0.0", {"position": v(0, -500) * mm});
            skPoint(sketch, "E26.33.0.1", {"position": v(15, -500) * mm});
            skPoint(sketch, "E26.33.0.2", {"position": v(30, -500) * mm});
            skPoint(sketch, "E26.33.0.3", {"position": v(45, -500) * mm});
            skPoint(sketch, "E26.33.0.4", {"position": v(60, -500) * mm});
            skPoint(sketch, "E26.33.0.5", {"position": v(75, -500) * mm});
            skPoint(sketch, "E26.33.0.6", {"position": v(90, -500) * mm});
            skPoint(sketch, "E26.34.0.0", {"position": v(0, -515) * mm});
            skPoint(sketch, "E26.34.0.1", {"position": v(15, -515) * mm});
            skPoint(sketch, "E26.34.0.2", {"position": v(30, -515) * mm});
            skPoint(sketch, "E26.34.0.3", {"position": v(45, -515) * mm});
            skPoint(sketch, "E26.34.0.4", {"position": v(60, -515) * mm});
            skPoint(sketch, "E26.34.0.5", {"position": v(75, -515) * mm});
            skPoint(sketch, "E26.34.0.6", {"position": v(90, -515) * mm});
            skPoint(sketch, "E26.35.0.0", {"position": v(0, -530) * mm});
            skPoint(sketch, "E26.35.0.1", {"position": v(15, -530) * mm});
            skPoint(sketch, "E26.35.0.2", {"position": v(30, -530) * mm});
            skPoint(sketch, "E26.35.0.3", {"position": v(45, -530) * mm});
            skPoint(sketch, "E26.35.0.4", {"position": v(60, -530) * mm});
            skPoint(sketch, "E26.35.0.5", {"position": v(75, -530) * mm});
            skPoint(sketch, "E26.35.0.6", {"position": v(90, -530) * mm});
            skPoint(sketch, "E26.36.0.0", {"position": v(0, -545) * mm});
            skPoint(sketch, "E26.36.0.1", {"position": v(15, -545) * mm});
            skPoint(sketch, "E26.36.0.2", {"position": v(30, -545) * mm});
            skPoint(sketch, "E26.36.0.3", {"position": v(45, -545) * mm});
            skPoint(sketch, "E26.36.0.4", {"position": v(60, -545) * mm});
            skPoint(sketch, "E26.36.0.5", {"position": v(75, -545) * mm});
            skPoint(sketch, "E26.36.0.6", {"position": v(90, -545) * mm});
            skPoint(sketch, "E26.37.0.0", {"position": v(0, -560) * mm});
            skPoint(sketch, "E26.37.0.1", {"position": v(15, -560) * mm});
            skPoint(sketch, "E26.37.0.2", {"position": v(30, -560) * mm});
            skPoint(sketch, "E26.37.0.3", {"position": v(45, -560) * mm});
            skPoint(sketch, "E26.37.0.4", {"position": v(60, -560) * mm});
            skPoint(sketch, "E26.37.0.5", {"position": v(75, -560) * mm});
            skPoint(sketch, "E26.37.0.6", {"position": v(90, -560) * mm});
            skPoint(sketch, "E26.38.0.0", {"position": v(0, -575) * mm});
            skPoint(sketch, "E26.38.0.1", {"position": v(15, -575) * mm});
            skPoint(sketch, "E26.38.0.2", {"position": v(30, -575) * mm});
            skPoint(sketch, "E26.38.0.3", {"position": v(45, -575) * mm});
            skPoint(sketch, "E26.38.0.4", {"position": v(60, -575) * mm});
            skPoint(sketch, "E26.38.0.5", {"position": v(75, -575) * mm});
            skPoint(sketch, "E26.38.0.6", {"position": v(90, -575) * mm});
            skPoint(sketch, "E26.39.0.0", {"position": v(0, -590) * mm});
            skPoint(sketch, "E26.39.0.1", {"position": v(15, -590) * mm});
            skPoint(sketch, "E26.39.0.2", {"position": v(30, -590) * mm});
            skPoint(sketch, "E26.39.0.3", {"position": v(45, -590) * mm});
            skPoint(sketch, "E26.39.0.4", {"position": v(60, -590) * mm});
            skPoint(sketch, "E26.39.0.5", {"position": v(75, -590) * mm});
            skPoint(sketch, "E26.39.0.6", {"position": v(90, -590) * mm});
            skLineSegment(sketch, "E26.direction1", {"start": v(0, -5) * mm, "end": v(0, -20) * mm, "construction": true});
            skSolve(sketch);
        }
        {
            var Q0;
            Q0=sQuery(id+"F8.wireOp",VERTEX,"E24");
            var Q1;
            Q1=sQuery(id+"F8.wireOp",VERTEX,"E26.1.0.0");
            var Q2;
            Q2=sQuery(id+"F8.wireOp",VERTEX,"E26.2.0.0");
            var Q3;
            Q3=sQuery(id+"F8.wireOp",VERTEX,"E25.1.0.0");
            var Q4;
            Q4=sQuery(id+"F8.wireOp",VERTEX,"E26.1.0.1");
            var Q5;
            Q5=sQuery(id+"F8.wireOp",VERTEX,"E26.2.0.1");
            var Q6;
            Q6=sQuery(id+"F8.wireOp",VERTEX,"E26.3.0.1");
            var Q7;
            Q7=sQuery(id+"F8.wireOp",VERTEX,"E25.2.0.0");
            var Q8;
            Q8=sQuery(id+"F8.wireOp",VERTEX,"E25.3.0.0");
            var Q9;
            Q9=sQuery(id+"F8.wireOp",VERTEX,"E25.4.0.0");
            var Q10;
            Q10=sQuery(id+"F8.wireOp",VERTEX,"E25.5.0.0");
            var Q11;
            Q11=sQuery(id+"F8.wireOp",VERTEX,"E25.6.0.0");
            var Q12;
            Q12=sQuery(id+"F8.wireOp",VERTEX,"E26.1.0.4");
            var Q13;
            Q13=sQuery(id+"F8.wireOp",VERTEX,"E26.1.0.3");
            var Q14;
            Q14=sQuery(id+"F8.wireOp",VERTEX,"E26.1.0.2");
            var Q15;
            Q15=sQuery(id+"F8.wireOp",VERTEX,"E26.2.0.4");
            var Q16;
            Q16=sQuery(id+"F8.wireOp",VERTEX,"E26.4.0.6");
            var Q17;
            Q17=sQuery(id+"F8.wireOp",VERTEX,"E26.3.0.6");
            var Q18;
            Q18=sQuery(id+"F8.wireOp",VERTEX,"E26.3.0.3");
            var Q19;
            Q19=sQuery(id+"F8.wireOp",VERTEX,"E26.2.0.3");
            var Q20;
            Q20=sQuery(id+"F8.wireOp",VERTEX,"E26.3.0.5");
            var Q21;
            Q21=sQuery(id+"F8.wireOp",VERTEX,"E26.4.0.5");
            var Q22;
            Q22=sQuery(id+"F8.wireOp",VERTEX,"E26.3.0.2");
            var Q23;
            Q23=sQuery(id+"F8.wireOp",VERTEX,"E26.2.0.2");
            var Q24;
            Q24=sQuery(id+"F8.wireOp",VERTEX,"E26.4.0.4");
            var Q25;
            Q25=sQuery(id+"F8.wireOp",VERTEX,"E26.3.0.4");
            var Q26;
            Q26=sQuery(id+"F8.wireOp",VERTEX,"E26.4.0.3");
            var Q27;
            Q27=sQuery(id+"F8.wireOp",VERTEX,"E26.4.0.2");
            var Q28;
            Q28=sQuery(id+"F8.wireOp",VERTEX,"E26.2.0.6");
            var Q29;
            Q29=sQuery(id+"F8.wireOp",VERTEX,"E26.1.0.6");
            var Q30;
            Q30=sQuery(id+"F8.wireOp",VERTEX,"E26.1.0.5");
            var Q31;
            Q31=sQuery(id+"F8.wireOp",VERTEX,"E26.2.0.5");
            var Q32;
            Q32=sQuery(id+"F8.wireOp",VERTEX,"E26.6.0.6");
            var Q33;
            Q33=sQuery(id+"F8.wireOp",VERTEX,"E26.6.0.5");
            var Q34;
            Q34=sQuery(id+"F8.wireOp",VERTEX,"E26.6.0.4");
            var Q35;
            Q35=sQuery(id+"F8.wireOp",VERTEX,"E26.7.0.6");
            var Q36;
            Q36=sQuery(id+"F8.wireOp",VERTEX,"E26.7.0.5");
            var Q37;
            Q37=sQuery(id+"F8.wireOp",VERTEX,"E26.8.0.6");
            var Q38;
            Q38=sQuery(id+"F8.wireOp",VERTEX,"E26.8.0.5");
            var Q39;
            Q39=sQuery(id+"F8.wireOp",VERTEX,"E26.5.0.6");
            var Q40;
            Q40=sQuery(id+"F8.wireOp",VERTEX,"E26.5.0.5");
            var Q41;
            Q41=sQuery(id+"F8.wireOp",VERTEX,"E26.5.0.4");
            var Q42;
            Q42=sQuery(id+"F8.wireOp",VERTEX,"E26.5.0.3");
            var Q43;
            Q43=sQuery(id+"F8.wireOp",VERTEX,"E26.20.0.6");
            var Q44;
            Q44=sQuery(id+"F8.wireOp",VERTEX,"E26.19.0.6");
            var Q45;
            Q45=sQuery(id+"F8.wireOp",VERTEX,"E26.14.0.6");
            var Q46;
            Q46=sQuery(id+"F8.wireOp",VERTEX,"E26.13.0.6");
            var Q47;
            Q47=sQuery(id+"F8.wireOp",VERTEX,"E26.12.0.6");
            var Q48;
            Q48=sQuery(id+"F8.wireOp",VERTEX,"E26.23.0.6");
            var Q49;
            Q49=sQuery(id+"F8.wireOp",VERTEX,"E26.21.0.6");
            var Q50;
            Q50=sQuery(id+"F8.wireOp",VERTEX,"E26.22.0.6");
            var Q51;
            Q51=sQuery(id+"F8.wireOp",VERTEX,"E26.16.0.6");
            var Q52;
            Q52=sQuery(id+"F8.wireOp",VERTEX,"E26.15.0.6");
            var Q53;
            Q53=sQuery(id+"F8.wireOp",VERTEX,"E26.9.0.6");
            var Q54;
            Q54=sQuery(id+"F8.wireOp",VERTEX,"E26.24.0.6");
            var Q55;
            Q55=sQuery(id+"F8.wireOp",VERTEX,"E26.25.0.6");
            var Q56;
            Q56=sQuery(id+"F8.wireOp",VERTEX,"E26.17.0.6");
            var Q57;
            Q57=sQuery(id+"F8.wireOp",VERTEX,"E26.18.0.6");
            var Q58;
            Q58=sQuery(id+"F8.wireOp",VERTEX,"E26.26.0.6");
            var Q59;
            Q59=sQuery(id+"F8.wireOp",VERTEX,"E26.10.0.6");
            var Q60;
            Q60=sQuery(id+"F8.wireOp",VERTEX,"E26.11.0.6");
            var Q61;
            Q61=sQuery(id+"F8.wireOp",VERTEX,"E26.35.0.6");
            var Q62;
            Q62=sQuery(id+"F8.wireOp",VERTEX,"E26.36.0.6");
            var Q63;
            Q63=sQuery(id+"F8.wireOp",VERTEX,"E26.30.0.6");
            var Q64;
            Q64=sQuery(id+"F8.wireOp",VERTEX,"E26.29.0.6");
            var Q65;
            Q65=sQuery(id+"F8.wireOp",VERTEX,"E26.28.0.6");
            var Q66;
            Q66=sQuery(id+"F8.wireOp",VERTEX,"E26.37.0.6");
            var Q67;
            Q67=sQuery(id+"F8.wireOp",VERTEX,"E26.38.0.6");
            var Q68;
            Q68=sQuery(id+"F8.wireOp",VERTEX,"E26.39.0.6");
            var Q69;
            Q69=sQuery(id+"F8.wireOp",VERTEX,"E26.31.0.6");
            var Q70;
            Q70=sQuery(id+"F8.wireOp",VERTEX,"E26.32.0.6");
            var Q71;
            Q71=sQuery(id+"F8.wireOp",VERTEX,"E26.33.0.6");
            var Q72;
            Q72=sQuery(id+"F8.wireOp",VERTEX,"E26.34.0.6");
            var Q73;
            Q73=sQuery(id+"F8.wireOp",VERTEX,"E26.27.0.6");
            var Q74;
            Q74=sQuery(id+"F8.wireOp",VERTEX,"E26.27.0.6");
            var Q75;
            Q75=sQuery(id+"F8.wireOp",VERTEX,"E26.28.0.6");
            var Q76;
            Q76=sQuery(id+"F8.wireOp",VERTEX,"E26.29.0.6");
            var Q77;
            Q77=sQuery(id+"F8.wireOp",VERTEX,"E26.30.0.6");
            var Q78;
            Q78=sQuery(id+"F8.wireOp",VERTEX,"E26.31.0.6");
            var Q79;
            Q79=sQuery(id+"F8.wireOp",VERTEX,"E26.32.0.6");
            var Q80;
            Q80=sQuery(id+"F8.wireOp",VERTEX,"E26.33.0.6");
            var Q81;
            Q81=sQuery(id+"F8.wireOp",VERTEX,"E26.34.0.6");
            var Q82;
            Q82=sQuery(id+"F8.wireOp",VERTEX,"E26.35.0.6");
            var Q83;
            Q83=sQuery(id+"F8.wireOp",VERTEX,"E26.36.0.6");
            var Q84;
            Q84=sQuery(id+"F8.wireOp",VERTEX,"E26.37.0.6");
            var Q85;
            Q85=sQuery(id+"F8.wireOp",VERTEX,"E26.38.0.6");
            var Q86;
            Q86=sQuery(id+"F8.wireOp",VERTEX,"E26.39.0.6");
            var Q87;
            Q87=makeQuery(id+"F1.opExtrude","SWEPT_BODY",BODY,{"disambiguationData":[OSD([sQuery(id+"F0.wireOp",EDGE,"E1.bottom"),sQuery(id+"F0.wireOp",EDGE,"E1.top"),sQuery(id+"F0.wireOp",EDGE,"E1.left"),sQuery(id+"F0.wireOp",EDGE,"E1.right"),sQuery(id+"F0.wireOp",EDGE,"E2"),sQuery(id+"F0.wireOp",EDGE,"E3"),sQuery(id+"F0.wireOp",EDGE,"E4"),sQuery(id+"F0.wireOp",EDGE,"E5"),sQuery(id+"F0.wireOp",EDGE,"E6"),sQuery(id+"F0.wireOp",EDGE,"E7"),sQuery(id+"F0.wireOp",EDGE,"E8"),sQuery(id+"F0.wireOp",EDGE,"E9.MirrorCS"),sQuery(id+"F0.wireOp",EDGE,"E10.MirrorCS"),sQuery(id+"F0.wireOp",EDGE,"E11.MirrorCS"),sQuery(id+"F0.wireOp",EDGE,"E13.trimOffspring"),sQuery(id+"F0.wireOp",EDGE,"E14.trimOffspring"),sQuery(id+"F0.wireOp",EDGE,"E16.trimOffspring"),sQuery(id+"F0.wireOp",EDGE,"E17.trimOffspring"),sQuery(id+"F0.wireOp",EDGE,"E20"),sQuery(id+"F0.wireOp",EDGE,"E21")])]});
            var Q88;
            Q88=makeQuery(id+"F2.opExtrude","SWEPT_BODY",BODY,{"disambiguationData":[OSD([sQuery(id+"F0.wireOp",EDGE,"E23.1.0.1"),sQuery(id+"F0.wireOp",EDGE,"E23.1.0.2"),sQuery(id+"F0.wireOp",EDGE,"E23.1.0.3"),sQuery(id+"F0.wireOp",EDGE,"E23.1.0.4"),sQuery(id+"F0.wireOp",EDGE,"E23.1.0.11"),sQuery(id+"F0.wireOp",EDGE,"E23.1.0.12"),sQuery(id+"F0.wireOp",EDGE,"E23.1.0.13"),sQuery(id+"F0.wireOp",EDGE,"E23.1.0.14"),sQuery(id+"F0.wireOp",EDGE,"E23.1.0.15"),sQuery(id+"F0.wireOp",EDGE,"E23.1.0.16"),sQuery(id+"F0.wireOp",EDGE,"E23.1.0.18"),sQuery(id+"F0.wireOp",EDGE,"E23.1.0.19"),sQuery(id+"F0.wireOp",EDGE,"E23.1.0.20"),sQuery(id+"F0.wireOp",EDGE,"E23.1.0.21"),sQuery(id+"F0.wireOp",EDGE,"E23.1.0.22"),sQuery(id+"F0.wireOp",EDGE,"E23.1.0.23"),sQuery(id+"F0.wireOp",EDGE,"E23.1.0.24"),sQuery(id+"F0.wireOp",EDGE,"E23.1.0.25"),sQuery(id+"F0.wireOp",EDGE,"E23.1.0.26"),sQuery(id+"F0.wireOp",EDGE,"E23.1.0.27")])]});
            var Q89;
            Q89=makeQuery(id+"F3.opExtrude","SWEPT_BODY",BODY,{"disambiguationData":[OSD([sQuery(id+"F0.wireOp",EDGE,"E23.2.0.1"),sQuery(id+"F0.wireOp",EDGE,"E23.2.0.2"),sQuery(id+"F0.wireOp",EDGE,"E23.2.0.3"),sQuery(id+"F0.wireOp",EDGE,"E23.2.0.4"),sQuery(id+"F0.wireOp",EDGE,"E23.2.0.11"),sQuery(id+"F0.wireOp",EDGE,"E23.2.0.12"),sQuery(id+"F0.wireOp",EDGE,"E23.2.0.13"),sQuery(id+"F0.wireOp",EDGE,"E23.2.0.14"),sQuery(id+"F0.wireOp",EDGE,"E23.2.0.15"),sQuery(id+"F0.wireOp",EDGE,"E23.2.0.16"),sQuery(id+"F0.wireOp",EDGE,"E23.2.0.18"),sQuery(id+"F0.wireOp",EDGE,"E23.2.0.19"),sQuery(id+"F0.wireOp",EDGE,"E23.2.0.20"),sQuery(id+"F0.wireOp",EDGE,"E23.2.0.21"),sQuery(id+"F0.wireOp",EDGE,"E23.2.0.22"),sQuery(id+"F0.wireOp",EDGE,"E23.2.0.23"),sQuery(id+"F0.wireOp",EDGE,"E23.2.0.24"),sQuery(id+"F0.wireOp",EDGE,"E23.2.0.25"),sQuery(id+"F0.wireOp",EDGE,"E23.2.0.26"),sQuery(id+"F0.wireOp",EDGE,"E23.2.0.27")])]});
            var Q90;
            Q90=makeQuery(id+"F4.opExtrude","SWEPT_BODY",BODY,{"disambiguationData":[OSD([sQuery(id+"F0.wireOp",EDGE,"E23.3.0.1"),sQuery(id+"F0.wireOp",EDGE,"E23.3.0.2"),sQuery(id+"F0.wireOp",EDGE,"E23.3.0.3"),sQuery(id+"F0.wireOp",EDGE,"E23.3.0.4"),sQuery(id+"F0.wireOp",EDGE,"E23.3.0.11"),sQuery(id+"F0.wireOp",EDGE,"E23.3.0.12"),sQuery(id+"F0.wireOp",EDGE,"E23.3.0.13"),sQuery(id+"F0.wireOp",EDGE,"E23.3.0.14"),sQuery(id+"F0.wireOp",EDGE,"E23.3.0.15"),sQuery(id+"F0.wireOp",EDGE,"E23.3.0.16"),sQuery(id+"F0.wireOp",EDGE,"E23.3.0.18"),sQuery(id+"F0.wireOp",EDGE,"E23.3.0.19"),sQuery(id+"F0.wireOp",EDGE,"E23.3.0.20"),sQuery(id+"F0.wireOp",EDGE,"E23.3.0.21"),sQuery(id+"F0.wireOp",EDGE,"E23.3.0.22"),sQuery(id+"F0.wireOp",EDGE,"E23.3.0.23"),sQuery(id+"F0.wireOp",EDGE,"E23.3.0.24"),sQuery(id+"F0.wireOp",EDGE,"E23.3.0.25"),sQuery(id+"F0.wireOp",EDGE,"E23.3.0.26"),sQuery(id+"F0.wireOp",EDGE,"E23.3.0.27")])]});
            var Q91;
            Q91=makeQuery(id+"F5.opExtrude","SWEPT_BODY",BODY,{"disambiguationData":[OSD([sQuery(id+"F0.wireOp",EDGE,"E23.4.0.1"),sQuery(id+"F0.wireOp",EDGE,"E23.4.0.2"),sQuery(id+"F0.wireOp",EDGE,"E23.4.0.3"),sQuery(id+"F0.wireOp",EDGE,"E23.4.0.4"),sQuery(id+"F0.wireOp",EDGE,"E23.4.0.11"),sQuery(id+"F0.wireOp",EDGE,"E23.4.0.12"),sQuery(id+"F0.wireOp",EDGE,"E23.4.0.13"),sQuery(id+"F0.wireOp",EDGE,"E23.4.0.14"),sQuery(id+"F0.wireOp",EDGE,"E23.4.0.15"),sQuery(id+"F0.wireOp",EDGE,"E23.4.0.16"),sQuery(id+"F0.wireOp",EDGE,"E23.4.0.18"),sQuery(id+"F0.wireOp",EDGE,"E23.4.0.19"),sQuery(id+"F0.wireOp",EDGE,"E23.4.0.20"),sQuery(id+"F0.wireOp",EDGE,"E23.4.0.21"),sQuery(id+"F0.wireOp",EDGE,"E23.4.0.22"),sQuery(id+"F0.wireOp",EDGE,"E23.4.0.23"),sQuery(id+"F0.wireOp",EDGE,"E23.4.0.24"),sQuery(id+"F0.wireOp",EDGE,"E23.4.0.25"),sQuery(id+"F0.wireOp",EDGE,"E23.4.0.26"),sQuery(id+"F0.wireOp",EDGE,"E23.4.0.27")])]});
            var Q92;
            Q92=makeQuery(id+"F6.opExtrude","SWEPT_BODY",BODY,{"disambiguationData":[OSD([sQuery(id+"F0.wireOp",EDGE,"E23.5.0.1"),sQuery(id+"F0.wireOp",EDGE,"E23.5.0.2"),sQuery(id+"F0.wireOp",EDGE,"E23.5.0.3"),sQuery(id+"F0.wireOp",EDGE,"E23.5.0.4"),sQuery(id+"F0.wireOp",EDGE,"E23.5.0.11"),sQuery(id+"F0.wireOp",EDGE,"E23.5.0.12"),sQuery(id+"F0.wireOp",EDGE,"E23.5.0.13"),sQuery(id+"F0.wireOp",EDGE,"E23.5.0.14"),sQuery(id+"F0.wireOp",EDGE,"E23.5.0.15"),sQuery(id+"F0.wireOp",EDGE,"E23.5.0.16"),sQuery(id+"F0.wireOp",EDGE,"E23.5.0.18"),sQuery(id+"F0.wireOp",EDGE,"E23.5.0.19"),sQuery(id+"F0.wireOp",EDGE,"E23.5.0.20"),sQuery(id+"F0.wireOp",EDGE,"E23.5.0.21"),sQuery(id+"F0.wireOp",EDGE,"E23.5.0.22"),sQuery(id+"F0.wireOp",EDGE,"E23.5.0.23"),sQuery(id+"F0.wireOp",EDGE,"E23.5.0.24"),sQuery(id+"F0.wireOp",EDGE,"E23.5.0.25"),sQuery(id+"F0.wireOp",EDGE,"E23.5.0.26"),sQuery(id+"F0.wireOp",EDGE,"E23.5.0.27")])]});
            var Q93;
            Q93=makeQuery(id+"F7.opExtrude","SWEPT_BODY",BODY,{"disambiguationData":[OSD([sQuery(id+"F0.wireOp",EDGE,"E23.6.0.1"),sQuery(id+"F0.wireOp",EDGE,"E23.6.0.2"),sQuery(id+"F0.wireOp",EDGE,"E23.6.0.3"),sQuery(id+"F0.wireOp",EDGE,"E23.6.0.4"),sQuery(id+"F0.wireOp",EDGE,"E23.6.0.11"),sQuery(id+"F0.wireOp",EDGE,"E23.6.0.12"),sQuery(id+"F0.wireOp",EDGE,"E23.6.0.13"),sQuery(id+"F0.wireOp",EDGE,"E23.6.0.14"),sQuery(id+"F0.wireOp",EDGE,"E23.6.0.15"),sQuery(id+"F0.wireOp",EDGE,"E23.6.0.16"),sQuery(id+"F0.wireOp",EDGE,"E23.6.0.18"),sQuery(id+"F0.wireOp",EDGE,"E23.6.0.19"),sQuery(id+"F0.wireOp",EDGE,"E23.6.0.20"),sQuery(id+"F0.wireOp",EDGE,"E23.6.0.21"),sQuery(id+"F0.wireOp",EDGE,"E23.6.0.22"),sQuery(id+"F0.wireOp",EDGE,"E23.6.0.23"),sQuery(id+"F0.wireOp",EDGE,"E23.6.0.24"),sQuery(id+"F0.wireOp",EDGE,"E23.6.0.25"),sQuery(id+"F0.wireOp",EDGE,"E23.6.0.26"),sQuery(id+"F0.wireOp",EDGE,"E23.6.0.27")])]});
            hole(context, id + "F9", {"style" : HoleStyle.C_BORE, "endStyle" : HoleEndStyle.THROUGH, "holeDiameter" : 2.4 * mm, "cBoreDiameter" : 4.2 * mm, "cBoreDepth" : 2.3 * mm, "majorDiameter" : 5 * mm, "isTappedThrough" : true, "tappedDepth" : 12 * mm, "tapClearance" : 3, "locations" : qUnion([Q0, Q1, Q2, Q3, Q4, Q5, Q6, Q7, Q8, Q9, Q10, Q11, Q12, Q13, Q14, Q15, Q16, Q17, Q18, Q19, Q20, Q21, Q22, Q23, Q24, Q25, Q26, Q27, Q28, Q29, Q30, Q31, Q32, Q33, Q34, Q35, Q36, Q37, Q38, Q39, Q40, Q41, Q42, Q43, Q44, Q45, Q46, Q47, Q48, Q49, Q50, Q51, Q52, Q53, Q54, Q55, Q56, Q57, Q58, Q59, Q60, Q61, Q62, Q63, Q64, Q65, Q66, Q67, Q68, Q69, Q70, Q71, Q72, Q73, Q74, Q75, Q76, Q77, Q78, Q79, Q80, Q81, Q82, Q83, Q84, Q85, Q86]), "scope" : qUnion([Q87, Q88, Q89, Q90, Q91, Q92, Q93])});
        }
    });
